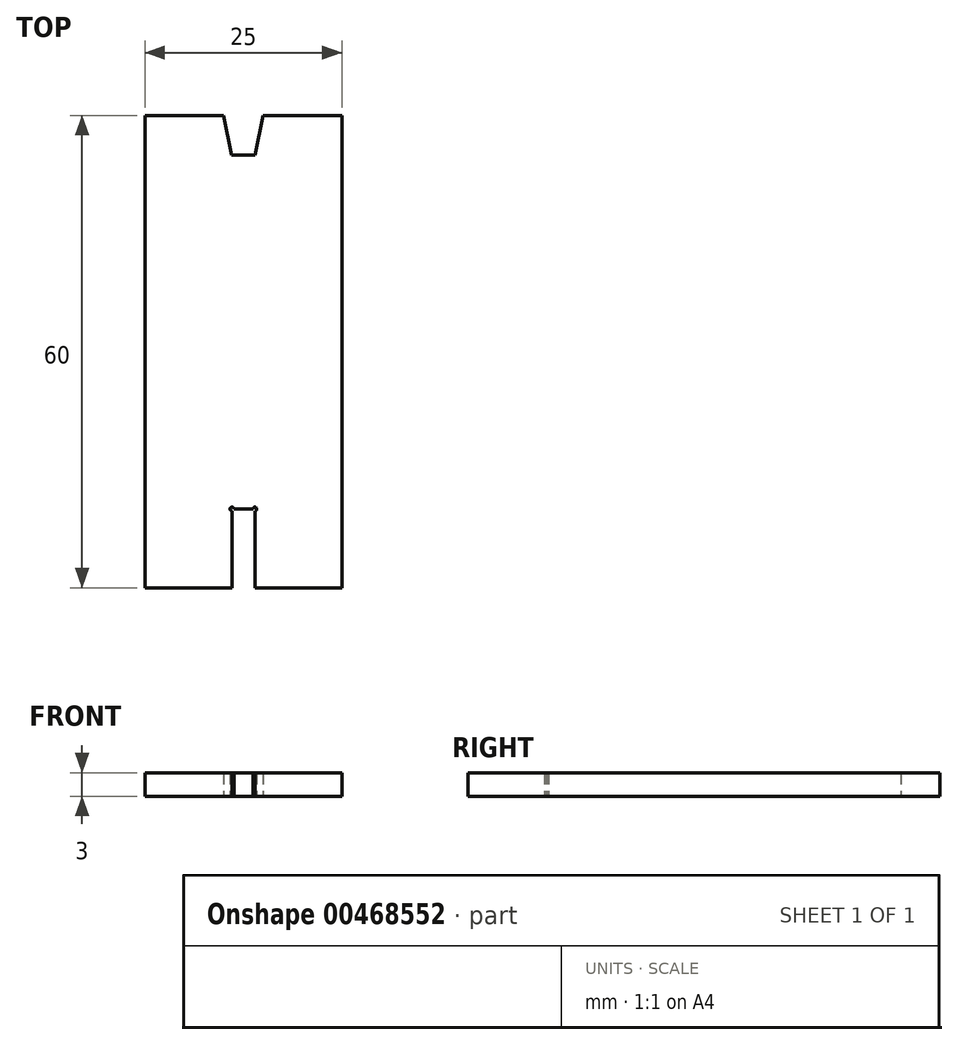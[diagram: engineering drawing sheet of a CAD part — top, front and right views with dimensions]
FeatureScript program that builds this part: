
annotation { "Feature Type Name" : "Feature", "Feature Type Description" : "" }
export const myFeature = defineFeature(function(context is Context, id is Id, definition is map)
    precondition{}
    {
        {
            var Q0;
            Q0=qCreatedBy(makeId("Top.planeOp"),FACE);
            var sketch = newSketch(context, id + "F0", { "sketchPlane" : qUnion([Q0])});
            skLineSegment(sketch, "E0.bottom", {"start": v(-12.5, 24.23) * mm, "end": v(12.5, 24.23) * mm});
            skLineSegment(sketch, "E0.top", {"start": v(-12.5, -35.77) * mm, "end": v(-1.45, -35.77) * mm});
            skLineSegment(sketch, "E0.left", {"start": v(-12.5, 24.23) * mm, "end": v(-12.5, -35.77) * mm});
            skLineSegment(sketch, "E0.right", {"start": v(12.5, 24.23) * mm, "end": v(12.5, -35.77) * mm});
            skPoint(sketch, "E1", {"position": v(0, 24.23) * mm});
            skLineSegment(sketch, "E2", {"start": v(-1.45, -35.77) * mm, "end": v(-1.45, -25.77) * mm});
            skLineSegment(sketch, "E3", {"start": v(-1.45, -25.77) * mm, "end": v(1.45, -25.77) * mm});
            skLineSegment(sketch, "E4", {"start": v(1.45, -25.77) * mm, "end": v(1.45, -35.77) * mm});
            skLineSegment(sketch, "E5.trimOffspring", {"start": v(1.45, -35.77) * mm, "end": v(12.5, -35.77) * mm});
            skLineSegment(sketch, "E6", {"start": v(-1.5, 19.23) * mm, "end": v(1.5, 19.23) * mm});
            skPoint(sketch, "E7", {"position": v(0, 19.23) * mm});
            skPoint(sketch, "E8", {"position": v(-2.5, 24.23) * mm});
            skPoint(sketch, "E9", {"position": v(2.5, 24.23) * mm});
            skLineSegment(sketch, "E10", {"start": v(-2.5, 24.23) * mm, "end": v(-1.5, 19.23) * mm});
            skLineSegment(sketch, "E11", {"start": v(1.5, 19.23) * mm, "end": v(2.5, 24.23) * mm});
            skLineSegment(sketch, "E12", {"start": v(-12.5, -35.77) * mm, "end": v(12.5, -35.77) * mm, "construction": true});
            skCircle(sketch, "E13", {"center": v(1.45, -25.77) * mm, "radius": 0.25 * mm});
            skCircle(sketch, "E14", {"center": v(-1.45, -25.77) * mm, "radius": 0.25 * mm});
            skSolve(sketch);
        }
        {
            var Q0;
            Q0=makeQuery(id+"F0.imprint","IMPRINT",FACE,{"disambiguationData":[TD([[makeQuery(id+"F0.imprint","IMPRINT",EDGE,{"derivedFrom":sQuery(id+"F0.wireOp",EDGE,"E0.top")}),1.0]])]});
            extrude(context, id + "F1", {"entities" : qUnion([Q0]), "depth" : 3 * mm, "offsetDistance" : 25 * mm});
        }
    });
